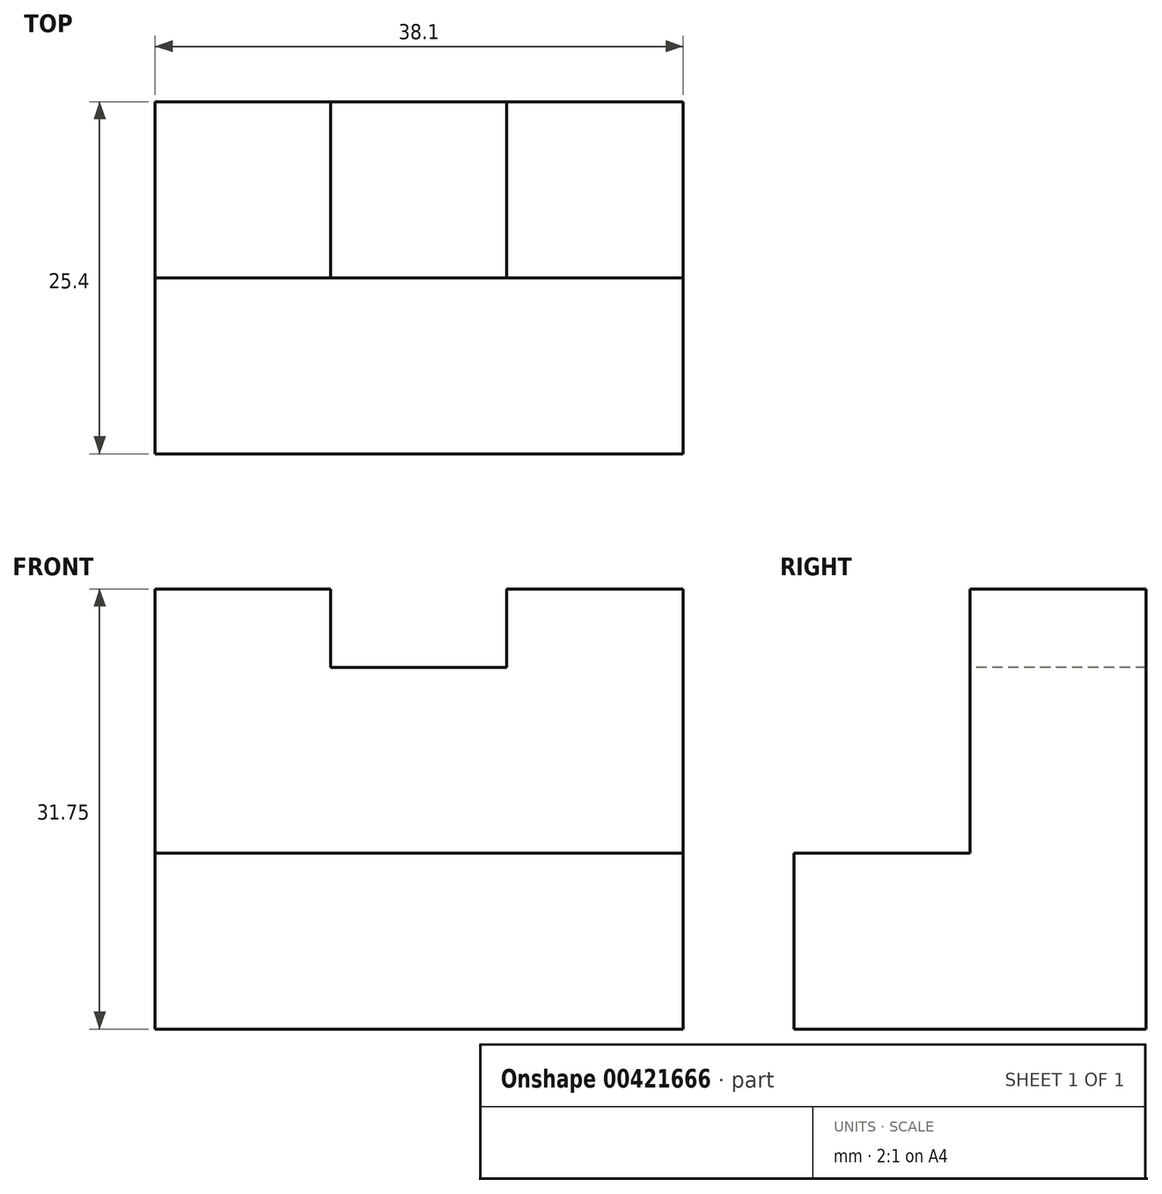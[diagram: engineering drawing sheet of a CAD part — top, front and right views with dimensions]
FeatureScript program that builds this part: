
annotation { "Feature Type Name" : "Feature", "Feature Type Description" : "" }
export const myFeature = defineFeature(function(context is Context, id is Id, definition is map)
    precondition{}
    {
        {
            var Q0;
            Q0=qCreatedBy(makeId("Right.planeOp"),FACE);
            var sketch = newSketch(context, id + "F0", { "sketchPlane" : qUnion([Q0])});
            skLineSegment(sketch, "E0", {"start": v(0, 0) * mm, "end": v(0, 12.7) * mm});
            skLineSegment(sketch, "E1", {"start": v(0, 12.7) * mm, "end": v(12.7, 12.7) * mm});
            skLineSegment(sketch, "E2", {"start": v(12.7, 12.7) * mm, "end": v(12.7, 31.75) * mm});
            skLineSegment(sketch, "E3", {"start": v(12.7, 31.75) * mm, "end": v(25.4, 31.75) * mm});
            skLineSegment(sketch, "E4", {"start": v(25.4, 31.75) * mm, "end": v(25.4, 0) * mm});
            skLineSegment(sketch, "E5", {"start": v(0, 0) * mm, "end": v(25.4, 0) * mm});
            skSolve(sketch);
        }
        {
            var Q0;
            Q0=makeQuery(id+"F0.imprint","IMPRINT",FACE,{"disambiguationData":[TD([[makeQuery(id+"F0.imprint","IMPRINT",EDGE,{"derivedFrom":sQuery(id+"F0.wireOp",EDGE,"E0")}),-1.0]])]});
            extrude(context, id + "F1", {"entities" : qUnion([Q0]), "depth" : 38.1 * mm});
        }
        {
            var Q0;
            Q0=qCreatedBy(makeId("Front.planeOp"),FACE);
            var sketch = newSketch(context, id + "F2", { "sketchPlane" : qUnion([Q0])});
            skLineSegment(sketch, "E6", {"start": v(12.65, 32.44) * mm, "end": v(12.65, 26.09) * mm});
            skLineSegment(sketch, "E7", {"start": v(12.65, 26.09) * mm, "end": v(25.35, 26.09) * mm});
            skLineSegment(sketch, "E8", {"start": v(25.35, 26.09) * mm, "end": v(25.35, 32.44) * mm});
            skLineSegment(sketch, "E9", {"start": v(25.35, 32.44) * mm, "end": v(12.65, 32.44) * mm});
            skSolve(sketch);
        }
        {
            var Q0;
            Q0=makeQuery(id+"F2.imprint","IMPRINT",FACE,{"disambiguationData":[TD([[makeQuery(id+"F2.imprint","IMPRINT",EDGE,{"derivedFrom":sQuery(id+"F2.wireOp",EDGE,"E6")}),1.0]])]});
            extrude(context, id + "F3", {"entities" : qUnion([Q0]), "operationType" : NewBodyOperationType.REMOVE, "oppositeDirection" : true, "depth" : 25.4 * mm});
        }
    });
